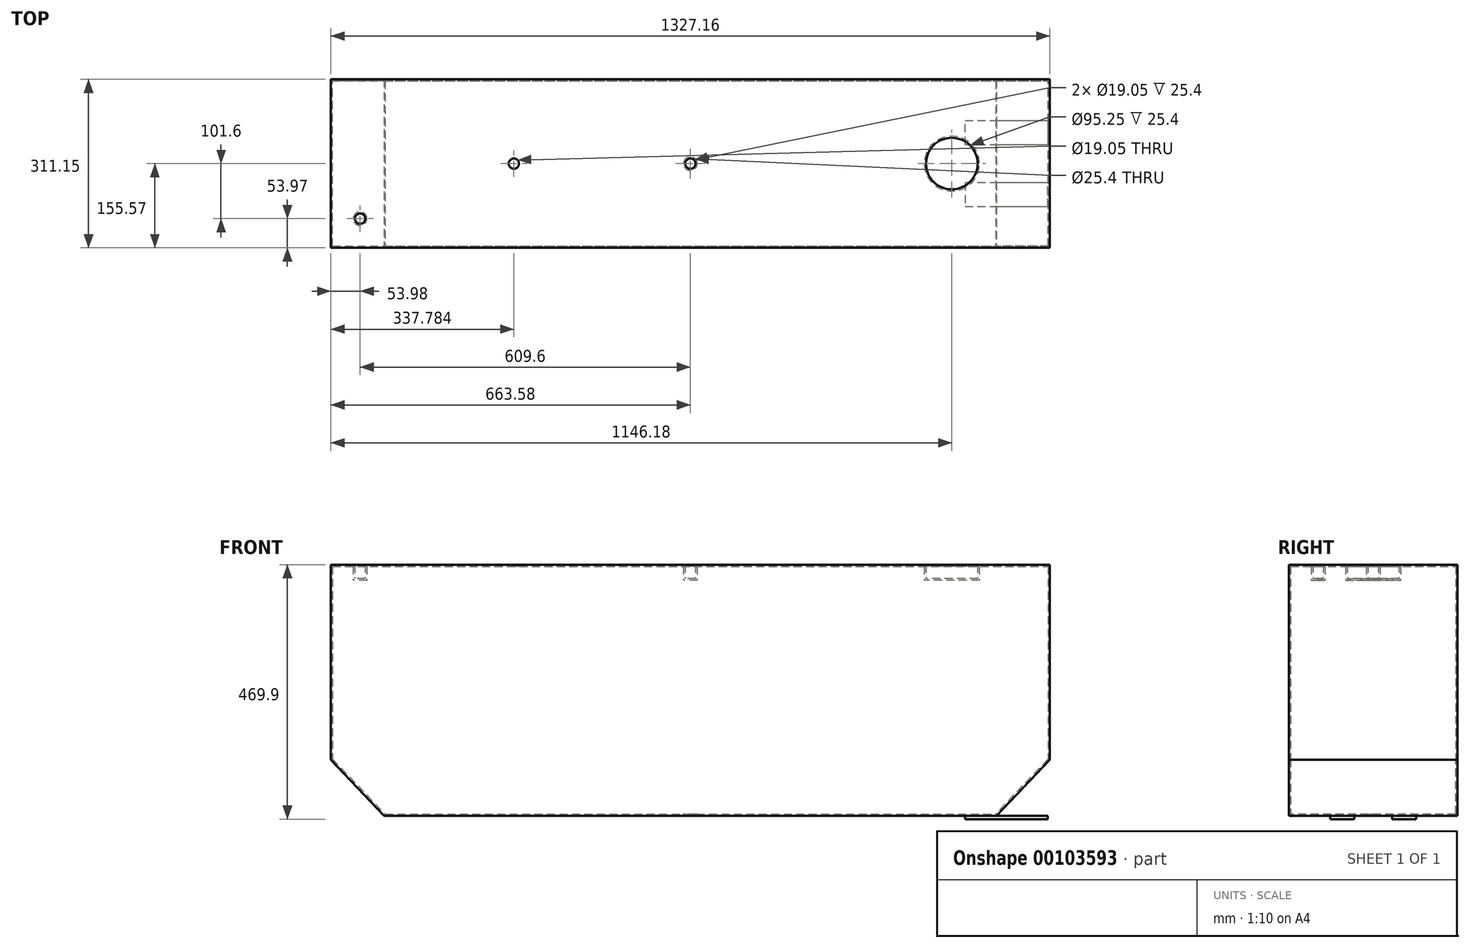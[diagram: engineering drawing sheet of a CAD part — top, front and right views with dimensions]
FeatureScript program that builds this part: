
annotation { "Feature Type Name" : "Feature", "Feature Type Description" : "" }
export const myFeature = defineFeature(function(context is Context, id is Id, definition is map)
    precondition{}
    {
        {
            var Q0;
            Q0=qCreatedBy(makeId("Front.planeOp"),FACE);
            var sketch = newSketch(context, id + "F0", { "sketchPlane" : qUnion([Q0])});
            skLineSegment(sketch, "E0.bottom", {"start": v(-660.4, 228.6) * mm, "end": v(660.4, 228.6) * mm});
            skLineSegment(sketch, "E0.top", {"start": v(-660.4, -228.6) * mm, "end": v(660.4, -228.6) * mm});
            skLineSegment(sketch, "E0.left", {"start": v(-660.4, 228.6) * mm, "end": v(-660.4, -228.6) * mm});
            skLineSegment(sketch, "E0.right", {"start": v(660.4, 228.6) * mm, "end": v(660.4, -228.6) * mm});
            skPoint(sketch, "E0.middle", {"position": v(0, 0) * mm});
            skSolve(sketch);
        }
        {
            var Q0;
            Q0 = qSketchRegion(id + "F0", true);
            extrude(context, id + "F1", {"entities" : qUnion([Q0]), "depth" : 304.8 * mm, "symmetric" : true});
        }
        {
            var Q0;
            Q0=makeQuery(id+"F1.opExtrude","SWEPT_FACE",FACE,{"disambiguationData":[OSD([sQuery(id+"F0.wireOp",EDGE,"E0.bottom")])]});
            var sketch = newSketch(context, id + "F2", { "sketchPlane" : qUnion([Q0])});
            skLineSegment(sketch, "E1", {"start": v(-660.4, 0) * mm, "end": v(660.4, 0) * mm, "construction": true});
            skCircle(sketch, "E2", {"center": v(482.6, 0) * mm, "radius": 50.8 * mm});
            skCircle(sketch, "E3", {"center": v(0, 0) * mm, "radius": 12.7 * mm});
            skCircle(sketch, "E4", {"center": v(-609.6, -101.6) * mm, "radius": 12.7 * mm});
            skSolve(sketch);
        }
        {
            var Q0;
            Q0 = qSketchRegion(id + "F2", true);
            extrude(context, id + "F3", {"entities" : qUnion([Q0]), "operationType" : NewBodyOperationType.REMOVE, "depth" : 50.8 * mm, "symmetric" : true});
        }
        {
            var Q0;
            Q0=makeQuery(id+"F1.opExtrude","CAP_FACE",FACE,{"disambiguationData":[OSD([sQuery(id+"F0.wireOp",EDGE,"E0.bottom"),sQuery(id+"F0.wireOp",EDGE,"E0.top"),sQuery(id+"F0.wireOp",EDGE,"E0.left"),sQuery(id+"F0.wireOp",EDGE,"E0.right")])],"isStart":false});
            var sketch = newSketch(context, id + "F4", { "sketchPlane" : qUnion([Q0])});
            skCircle(sketch, "E5", {"center": v(-508, -177.8) * mm, "radius": 12.7 * mm});
            skSolve(sketch);
        }
        {
            var Q0;
            Q0=makeQuery(id+"F4.imprint","IMPRINT",FACE,{"disambiguationData":[TD([[makeQuery(id+"F4.imprint","IMPRINT",EDGE,{"derivedFrom":sQuery(id+"F4.wireOp",EDGE,"E5")}),-1.0]])]});
            var sketch = newSketch(context, id + "F5", { "sketchPlane" : qUnion([Q0])});
            skLineSegment(sketch, "E6", {"start": v(-660.62, -126.75) * mm, "end": v(-559.02, -233.43) * mm});
            skLineSegment(sketch, "E7", {"start": v(-559.02, -233.43) * mm, "end": v(-660.62, -233.43) * mm});
            skLineSegment(sketch, "E8", {"start": v(-660.62, -233.43) * mm, "end": v(-660.62, -126.75) * mm});
            skLineSegment(sketch, "E9", {"start": v(0, 230.33) * mm, "end": v(0, -229.72) * mm, "construction": true});
            skLineSegment(sketch, "E10.MirrorCS", {"start": v(559.02, -233.43) * mm, "end": v(660.62, -233.43) * mm});
            skLineSegment(sketch, "E11.MirrorCS", {"start": v(660.62, -233.43) * mm, "end": v(660.62, -126.75) * mm});
            skLineSegment(sketch, "E12.MirrorCS", {"start": v(660.62, -126.75) * mm, "end": v(559.02, -233.43) * mm});
            skSolve(sketch);
        }
        {
            var Q0;
            Q0 = qSketchRegion(id + "F5", true);
            var Q1;
            Q1=makeQuery(id+"F1.opExtrude","CAP_FACE",FACE,{"disambiguationData":[OSD([sQuery(id+"F0.wireOp",EDGE,"E0.bottom"),sQuery(id+"F0.wireOp",EDGE,"E0.top"),sQuery(id+"F0.wireOp",EDGE,"E0.left"),sQuery(id+"F0.wireOp",EDGE,"E0.right")])],"isStart":true});
            extrude(context, id + "F6", {"entities" : qUnion([Q0]), "operationType" : NewBodyOperationType.REMOVE, "endBound" : BoundingType.UP_TO_SURFACE, "oppositeDirection" : true, "endBoundEntityFace" : qUnion([Q1]), "depth" : 25.4 * mm});
        }
        {
            var Q0;
            Q0=makeQuery(id+"F1.opExtrude","SWEPT_FACE",FACE,{"disambiguationData":[OSD([sQuery(id+"F0.wireOp",EDGE,"E0.bottom")])]});
            var Q1;
            Q1=makeQuery(id+"F1.opExtrude","CAP_FACE",FACE,{"disambiguationData":[OSD([sQuery(id+"F0.wireOp",EDGE,"E0.bottom"),sQuery(id+"F0.wireOp",EDGE,"E0.top"),sQuery(id+"F0.wireOp",EDGE,"E0.left"),sQuery(id+"F0.wireOp",EDGE,"E0.right")])],"isStart":false});
            var Q2;
            Q2=makeQuery(id+"F1.opExtrude","SWEPT_FACE",FACE,{"disambiguationData":[OSD([sQuery(id+"F0.wireOp",EDGE,"E0.left")])]});
            var Q3;
            Q3=makeQuery(id+"F6.boolean.opBoolean","COPY",FACE,{"derivedFrom":makeQuery(id+"F6.opExtrude","SWEPT_FACE",FACE,{"disambiguationData":[OSD([sQuery(id+"F5.wireOp",EDGE,"E6")])]})});
            var Q4;
            Q4=makeQuery(id+"F1.opExtrude","CAP_FACE",FACE,{"disambiguationData":[OSD([sQuery(id+"F0.wireOp",EDGE,"E0.bottom"),sQuery(id+"F0.wireOp",EDGE,"E0.top"),sQuery(id+"F0.wireOp",EDGE,"E0.left"),sQuery(id+"F0.wireOp",EDGE,"E0.right")])],"isStart":true});
            var Q5;
            Q5=makeQuery(id+"F1.opExtrude","SWEPT_FACE",FACE,{"disambiguationData":[OSD([sQuery(id+"F0.wireOp",EDGE,"E0.top")])]});
            var Q6;
            Q6=makeQuery(id+"F6.boolean.opBoolean","COPY",FACE,{"derivedFrom":makeQuery(id+"F6.opExtrude","SWEPT_FACE",FACE,{"disambiguationData":[OSD([sQuery(id+"F5.wireOp",EDGE,"E12.MirrorCS")])]})});
            var Q7;
            Q7=makeQuery(id+"F1.opExtrude","SWEPT_FACE",FACE,{"disambiguationData":[OSD([sQuery(id+"F0.wireOp",EDGE,"E0.right")])]});
            var Q8;
            Q8=makeQuery(id+"F1.opExtrude","SWEPT_BODY",BODY,{"disambiguationData":[OSD([sQuery(id+"F0.wireOp",EDGE,"E0.bottom"),sQuery(id+"F0.wireOp",EDGE,"E0.top"),sQuery(id+"F0.wireOp",EDGE,"E0.left"),sQuery(id+"F0.wireOp",EDGE,"E0.right")])]});
            shell(context, id + "F7", {"isHollow" : true, "entities" : qUnion([Q0, Q1, Q2, Q3, Q4, Q5, Q6, Q7]), "parts" : qUnion([Q8]), "thickness" : 3.17 * mm, "oppositeDirection" : true});
        }
        {
            var Q0;
            Q0=makeQuery(id+"F1.opExtrude","SWEPT_FACE",FACE,{"disambiguationData":[OSD([sQuery(id+"F0.wireOp",EDGE,"E0.top")])]});
            var sketch = newSketch(context, id + "F8", { "sketchPlane" : qUnion([Q0])});
            skLineSegment(sketch, "E13.bottom", {"start": v(506.95, -79.37) * mm, "end": v(659.35, -79.37) * mm});
            skLineSegment(sketch, "E13.top", {"start": v(506.95, -34.92) * mm, "end": v(659.35, -34.92) * mm});
            skLineSegment(sketch, "E13.right", {"start": v(659.35, -79.37) * mm, "end": v(659.35, -34.92) * mm});
            skLineSegment(sketch, "E14", {"start": v(-564.98, 0) * mm, "end": v(564.98, 0) * mm, "construction": true});
            skLineSegment(sketch, "E15", {"start": v(506.95, -34.92) * mm, "end": v(506.95, -79.37) * mm});
            skLineSegment(sketch, "E16.MirrorCS", {"start": v(659.35, 79.37) * mm, "end": v(659.35, 34.92) * mm});
            skLineSegment(sketch, "E17.MirrorCS", {"start": v(506.95, 79.38) * mm, "end": v(659.35, 79.38) * mm});
            skLineSegment(sketch, "E18.MirrorCS", {"start": v(506.95, 34.92) * mm, "end": v(659.35, 34.92) * mm});
            skLineSegment(sketch, "E19.MirrorCS", {"start": v(506.95, 34.92) * mm, "end": v(506.95, 79.38) * mm});
            skSolve(sketch);
        }
        {
            var Q0;
            Q0 = qSketchRegion(id + "F8", true);
            extrude(context, id + "F9", {"entities" : qUnion([Q0]), "operationType" : NewBodyOperationType.ADD, "depth" : 6.35 * mm});
        }
        {
            var Q0;
            {var subQ7=sQuery(id+"F8.wireOp",EDGE,"E15");Q0=makeQuery(id+"F8.imprint","IMPRINT",FACE,{"disambiguationData":[TD([[makeQuery(id+"F8.imprint","IMPRINT",EDGE,{"derivedFrom":subQ7}),-1.0]])]});}
            var sketch = newSketch(context, id + "F10", { "sketchPlane" : qUnion([Q0])});
            skCircle(sketch, "E20", {"center": v(-488.78, 79.38) * mm, "radius": 12.7 * mm});
            skCircle(sketch, "E21", {"center": v(0, 0) * mm, "radius": 12.7 * mm});
            skSolve(sketch);
        }
        {
            var Q0;
            Q0=makeQuery(id+"F1.opExtrude","SWEPT_FACE",FACE,{"disambiguationData":[OSD([sQuery(id+"F0.wireOp",EDGE,"E0.bottom")])]});
            var sketch = newSketch(context, id + "F11", { "sketchPlane" : qUnion([Q0])});
            skCircle(sketch, "E22", {"center": v(-325.8, 0) * mm, "radius": 9.53 * mm});
            skSolve(sketch);
        }
        {
            var Q0;
            Q0 = qSketchRegion(id + "F11", true);
            extrude(context, id + "F12", {"entities" : qUnion([Q0]), "operationType" : NewBodyOperationType.REMOVE, "depth" : 25.4 * mm, "symmetric" : true});
        }
        {
            var Q0;
            Q0=makeQuery(id+"F10.imprint","IMPRINT",FACE,{"disambiguationData":[TD([[makeQuery(id+"F10.imprint","IMPRINT",EDGE,{"derivedFrom":sQuery(id+"F10.wireOp",EDGE,"E21")}),1.0]])]});
            extrude(context, id + "F13", {"entities" : qUnion([Q0]), "operationType" : NewBodyOperationType.REMOVE, "depth" : 25.4 * mm, "symmetric" : true});
        }
    });
